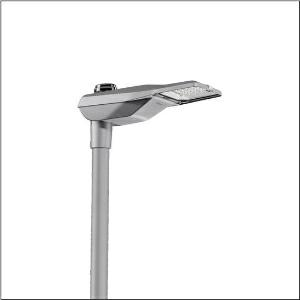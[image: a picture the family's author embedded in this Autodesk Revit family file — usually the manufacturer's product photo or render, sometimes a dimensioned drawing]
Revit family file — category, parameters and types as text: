
# Revit family: streetlight_sl_21_micro___pl52_5xe5h47n08db_21d1
name_source: partatom
category: Lighting Fixtures
units: mm (PartAtom-declared; Revit-internal decimal feet)

## family parameters
Cut with Voids When Loaded = No
Host = Face
Light Source = No
Part Type = Normal
Room Calculation Point = No
Round Connector Dimension = Use Diameter
Shared = No

## types (1)
- --- (1 x LED, 5230 lm, 39.1 W, 4000K)
    Apparent Load = 39 VA
    CIE Flux Codes = 27 59 98 100 100
    Color Rendering = 70
    Color Temperature = 4000K
    Default Elevation = 1800 mm
    Description = Streetlight SL 21 micro, mast luminaire, primary light control with lens, of PMMA, primary optical cover: cover, of toughened safety glass, transparent, light distribution: PL52, light emission: direct distribution, primary light characteristic: asymmetric, installation type: post-top, LED, 3G 1.5mm², High Power LED, rated luminous flux: 5.230lm, luminous efficacy: 134lm/W, light colour: 740, colour temperature: 4000K, control: overheat protection, presetting dimming linear, constant luminous flux control, time-dependent luminous flux control, flexible luminous flux parameterisation, mains connection: 230..240V, AC, 50/60Hz, connection cable pre-assembled, cable length: 6,5m, wiring characteristics: H07RN-F, start of lifetime: 39W, end of service life: 41W, reduction: 18W, luminaire housing, of diecast aluminium (EN AC-44300), powder-coated, Siteco® metallic grey (DB 702S), corrosivity category C5 mid according to DIN EN ISO 12944, multi-level sealing system, sealing non-destructively replaceable, inclination adjustable: 0°, 5°, 10°, 15°, length: 528mm, width: 235mm, height: 110mm, spigot size: 76/60mm (post-top), protection rating (complete): IP66, insulation class (complete): insulation class I (protective earthing), certification: CE, ENEC, ENEC+, VDE, impact resistance: IK09, permissible operating ambient temperature for outdoor applications: -40..+50°C, standard-compliant lighting for roads and squares, packaging unit: 1 piece

Light Distribution: PL52
    Height = 110 mm
    Lamp = 1 x LED
    Lamp Light Flux = 5230 lm
    Lamp Power = 39.1 W
    Lamp count = 1
    Length = 528 mm
    Luminous efficacy = 134 lm/W
    Manufacturer = Siteco
    ModVariant = No
    Model = 5XE5H47N08DB
    Number of Poles = 1
    OnlyDefault = Yes
    Power Factor = 1
    Product Name = Streetlight SL 21 micro | PL52
    Product group = mast luminaire | pylon top
    ProductGroupID = 6100
    Protection Class = Protection class I
    Protection Degree = IP 66
    RLX_Detail_Level = 1
    RLX_Emergency_Light_Flux = 0 lm
    RLX_Emergency_Type = 0
    RLX_Emergency_Type_DB = No
    RlxData = <blob elided: 108201 chars, md5=f9a224a0>
    Socket = socket
    Standby Power = 0 W
    System Light Flux = 5230 lm
    System Power = 39 W
    Type Comments = factory setting: luminous flux: 100 % | dim-lin: 254 | 765 mA
    Type Image = l_1294375.jpg
    URL = http://relux.com
    VarID = @adj_086499
    Voltage = 0 V
    Weight = 0.00 kg
    Width = 235 mm

## geometry (parser evidence)
native form markers: Blend x4, Sweep x11
no freeform markers — native parametric forms only
